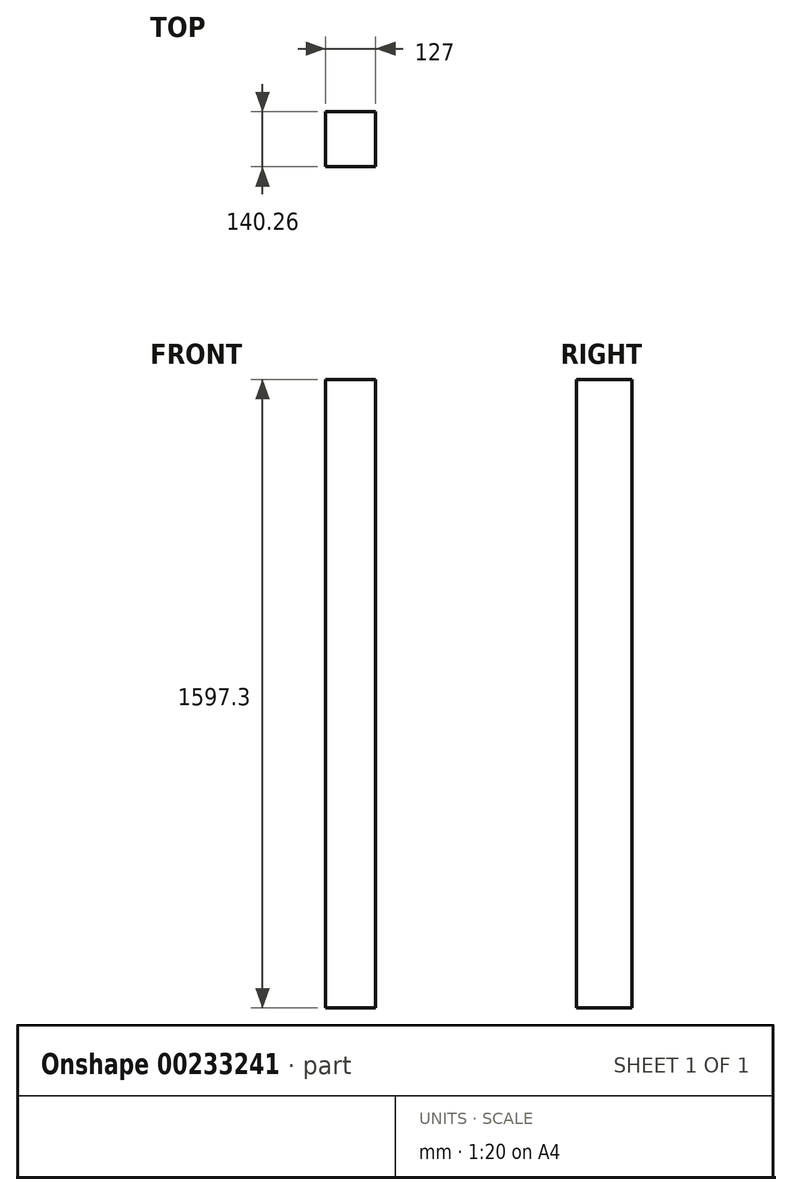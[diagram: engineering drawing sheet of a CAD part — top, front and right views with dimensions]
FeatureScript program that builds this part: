
annotation { "Feature Type Name" : "Feature", "Feature Type Description" : "" }
export const myFeature = defineFeature(function(context is Context, id is Id, definition is map)
    precondition{}
    {
        {
            var Q0;
            Q0=qCreatedBy(makeId("Right.planeOp"),FACE);
            var sketch = newSketch(context, id + "F0", { "sketchPlane" : qUnion([Q0])});
            skLineSegment(sketch, "E0.bottom", {"start": v(667.74, 134.55) * mm, "end": v(808, 134.55) * mm});
            skLineSegment(sketch, "E0.top", {"start": v(667.74, -1462.75) * mm, "end": v(808, -1462.75) * mm});
            skLineSegment(sketch, "E0.left", {"start": v(667.74, 134.55) * mm, "end": v(667.74, -1462.75) * mm});
            skLineSegment(sketch, "E0.right", {"start": v(808, 134.55) * mm, "end": v(808, -1462.75) * mm});
            skSolve(sketch);
        }
        {
            var Q0;
            Q0=makeQuery(id+"F0.imprint","IMPRINT",FACE,{"disambiguationData":[TD([[makeQuery(id+"F0.imprint","IMPRINT",EDGE,{"derivedFrom":sQuery(id+"F0.wireOp",EDGE,"E0.bottom")}),-1.0]])]});
            extrude(context, id + "F1", {"entities" : qUnion([Q0]), "depth" : 127 * mm});
        }
    });
